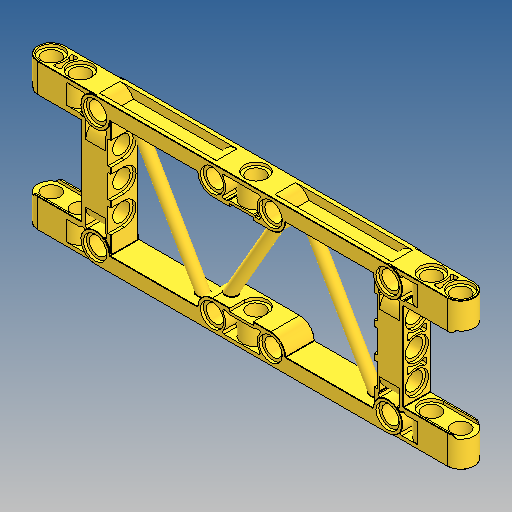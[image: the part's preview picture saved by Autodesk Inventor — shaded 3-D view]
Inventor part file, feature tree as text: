
AUTODESK INVENTOR PART (.ipt)
format: ipt  version: 2025 (Build 290162010, 162A)  size: 1,341,952 bytes
history: native  units: mm
features: sketch x17, extrude x14, delete_face x3, mirror x3, revolve x3, hole x2, fillet x2
ambient origin geometry x8: Origin, YZ Plane, XZ Plane, XY Plane, X Axis, Y Axis, Z Axis, Center Point
bodies: Volumenkörper1 (feature_tree)
feature tree (44):
  extrude  "Extrusion1"  Depth=8.0mm
  extrude  "Extrusion2"  Depth=44.0mm
  extrude  "Extrusion3"  Depth=36.0mm
  extrude  "Extrusion4"  Depth=4.0mm
  delete_face  "Fläche löschen1"
  extrude  "Extrusion5"  Depth=4.0mm TaperAngle=0.0deg
  extrude  "Extrusion6"  Depth=0.8mm TaperAngle=0.0deg
  extrude  "Extrusion7"  Depth=0.3mm TaperAngle=0.0deg
  hole  "Bohrung1"  [1 undecoded]
  hole  "Bohrung2"  [1 undecoded]
  extrude  "Extrusion8"  Depth=8.0mm
  extrude  "Extrusion9"  Depth=0.4mm
  extrude  "Extrusion10"  Depth=1.1mm
  fillet  "Rundung1"  Radius=8.0mm
  mirror  "Spiegeln1"
  extrude  "Extrusion11"  Depth=3.6mm TaperAngle=0.0deg
  extrude  "Extrusion12"  Depth=0.4mm
  extrude  "Extrusion13"  TaperAngle=45.0deg  [1 undecoded]
  extrude  "Extrusion14"  TaperAngle=45.0deg  [1 undecoded]
  mirror  "Spiegeln2"
  mirror  "Spiegeln3"
  sketch  "Skizze15"  dims[d39=3.5mm d40=45.0deg]
  revolve  "Umdrehung1"
  revolve  "Umdrehung2"
  revolve  "Umdrehung3"
  delete_face  "Fläche löschen2"
  delete_face  "Fläche löschen3"
  fillet  "Rundung2"  Radius=0.4mm
  sketch  "Skizze1"  dims[d0=12.0mm d1=8.0mm]
  sketch  "Skizze2"  dims[d2=8.0mm d3=44.0mm]
  sketch  "Skizze3"  dims[d4=8.0mm d5=36.0mm]
  sketch  "Skizze4"  dims[d6=0.1mm d7=4.0mm]
  sketch  "Skizze5"  dims[d8=4.8mm d9=4.0mm d10=0.0mm]
  sketch  "Skizze6"  dims[d11=6.4mm d12=0.8mm d13=0.0mm]
  sketch  "Skizze7"  dims[d14=0.1mm d15=0.3mm d16=0.0mm]
  sketch  "Skizze8"  dims[d17=16.0mm d18=8.0mm d19=0.0mm]
  sketch  "Skizze9"  dims[d20=3.7mm d21=1.1mm]
  sketch  "Skizze10"  dims[d22=1.1mm d23=8.0mm]
  sketch  "Skizze11"  dims[d24=3.7mm d25=0.4mm]
  sketch  "Skizze12"  dims[d26=1.1mm d27=1.1mm d28=8.0mm]
  sketch  "Skizze13"  dims[d30=3.6mm d31=0.0mm d33=3.6mm d34=0.0mm]
  sketch  "Skizze14"  dims[d35=10.0mm d36=0.0mm d37=0.4mm d38=0.4mm]
  sketch  "Skizze16"  dims[d41=45.0deg d42=45.0deg d43=0.4mm]
  sketch  "Skizze17"  dims[d44=0.4mm d45=4.8mm d46=6.0mm d47=6.4mm d48=0.8mm d49=90.0deg d50=8.0mm d51=20.594885mm d52=4.8mm d53=6.0mm d54=6.4mm d55=0.8mm d56=90.0deg d57=8.0mm d58=20.594885mm d59=2.4mm d60=2.8mm d61=0.0mm d62=1.1mm d63=3.7mm d64=0.4mm d65=6.0mm d66=0.0mm d67=3.7mm d68=1.1mm d69=0.4mm d70=10.0mm d71=0.0mm d72=0.1mm d73=0.8mm d74=0.0mm d75=0.8mm d76=0.0mm d77=60.0deg d78=41.0mm d79=20.5mm d80=60.0deg d81=1.5mm d82=90.0deg d83=90.0deg d84=90.0deg d85=0.1mm d86=0.8mm d87=0.0mm d88=0.0mm d89=0.0mm]
note: 4 required parameter values undecoded (feature->parameter linkage not recoverable at this tier; creation-order binding heuristic only, values carry confidence <= 0.55)
